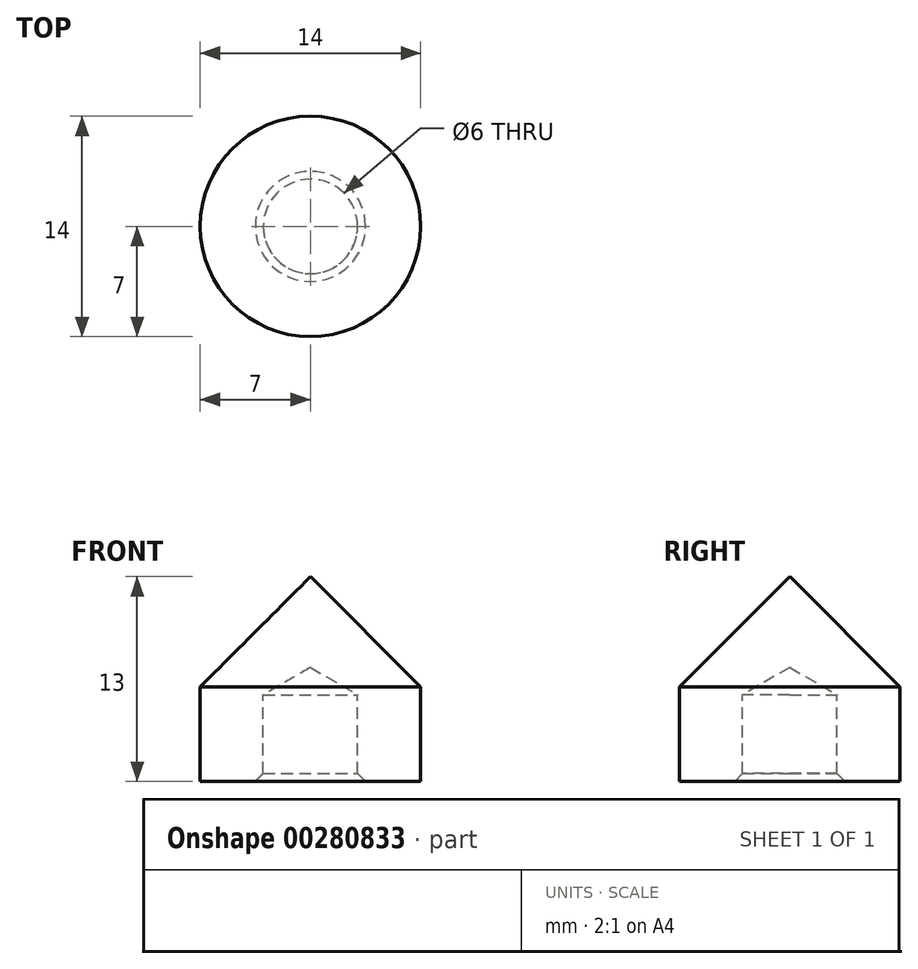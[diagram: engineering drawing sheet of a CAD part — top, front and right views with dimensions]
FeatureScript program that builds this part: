
annotation { "Feature Type Name" : "Feature", "Feature Type Description" : "" }
export const myFeature = defineFeature(function(context is Context, id is Id, definition is map)
    precondition{}
    {
        {
            var Q0;
            Q0=qCreatedBy(makeId("Front.planeOp"),FACE);
            var sketch = newSketch(context, id + "F0", { "sketchPlane" : qUnion([Q0])});
            skLineSegment(sketch, "E0", {"start": v(0, 13) * mm, "end": v(7, 6) * mm});
            skLineSegment(sketch, "E1", {"start": v(7, 6) * mm, "end": v(7, 0) * mm});
            skLineSegment(sketch, "E2", {"start": v(7, 0) * mm, "end": v(3, 0) * mm});
            skLineSegment(sketch, "E3", {"start": v(0, 7.23) * mm, "end": v(0, 13) * mm});
            skLineSegment(sketch, "E4", {"start": v(0, 19.54) * mm, "end": v(0, -5.08) * mm, "construction": true});
            skLineSegment(sketch, "E5", {"start": v(3, 0) * mm, "end": v(3, 5.5) * mm});
            skLineSegment(sketch, "E6", {"start": v(3, 5.5) * mm, "end": v(0, 7.23) * mm});
            skSolve(sketch);
        }
        {
            var Q0;
            Q0=makeQuery(id+"F0.imprint","IMPRINT",FACE,{"disambiguationData":[TD([[makeQuery(id+"F0.imprint","IMPRINT",EDGE,{"derivedFrom":sQuery(id+"F0.wireOp",EDGE,"E0")}),-1.0]])]});
            var Q1;
            Q1=sQuery(id+"F0.wireOp",EDGE,"E4");
            revolve(context, id + "F1", {"entities" : qUnion([Q0]), "axis" : qUnion([Q1]), "revolveType" : RevolveType.FULL});
        }
        {
            var Q0;
            Q0=makeQuery(id+"F1.opRevolve","SWEPT_EDGE",EDGE,{"disambiguationData":[OSD([sQuery(id+"F0.wireOp",EDGE,"E2"),sQuery(id+"F0.wireOp",EDGE,"E5")])]});
            chamfer(context, id + "F2", {"entities" : qUnion([Q0]), "width" : 0.5 * mm, "tangentPropagation" : true});
        }
    });
